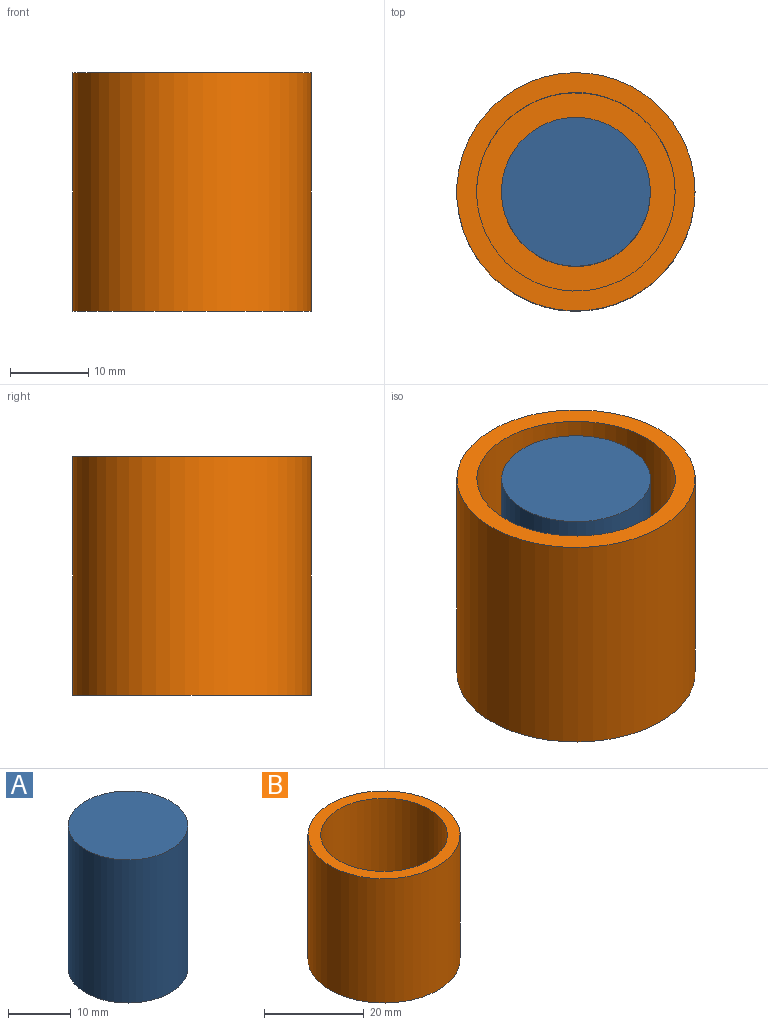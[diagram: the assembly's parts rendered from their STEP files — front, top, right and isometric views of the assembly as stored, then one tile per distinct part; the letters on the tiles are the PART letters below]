
ASSEMBLY  parts=2 mates=1
PART A: 3 faces, bbox 19.1x19.1x27.9 mm
  f0: cylinder r=9.53mm len=27.94mm, axis (0,0,-1), area 1672.1mm2, adj f1,f2
  f1: plane 19.05x19.05mm, normal (0,0,1), area 285mm2, adj f0
  f2: plane 19.05x19.05mm, normal (0,0,-1), area 285mm2, adj f0
PART B: 7 faces, bbox 30.5x30.5x30.5 mm
  f0: plane 25.4x25.4mm, normal (0,0,1), area 221.7mm2, adj f1,f5
  f1: cylinder r=12.7mm len=25.4mm, axis (0,0,-1), area 2026.8mm2, adj f0,f3
  f2: cylinder r=15.24mm len=30.48mm, axis (0,0,-1), area 2918.6mm2, adj f3,f4
  f3: plane 30.48x30.48mm, normal (0,0,1), area 223mm2, adj f1,f2
  f4: plane 30.48x30.48mm, normal (0,0,-1), area 729.7mm2, adj f2
  f5: cylinder r=9.53mm len=19.05mm, axis (0,0,1), area 152mm2, adj f0,f6
  f6: plane 19.05x19.05mm, normal (0,0,1), area 285mm2, adj f5
PLACE A t=(0,0,16.51)mm
PLACE B at identity
MATE planar A.f0 <-> B.f1  axis (0,0,-1) through (0,0,2.54)mm
